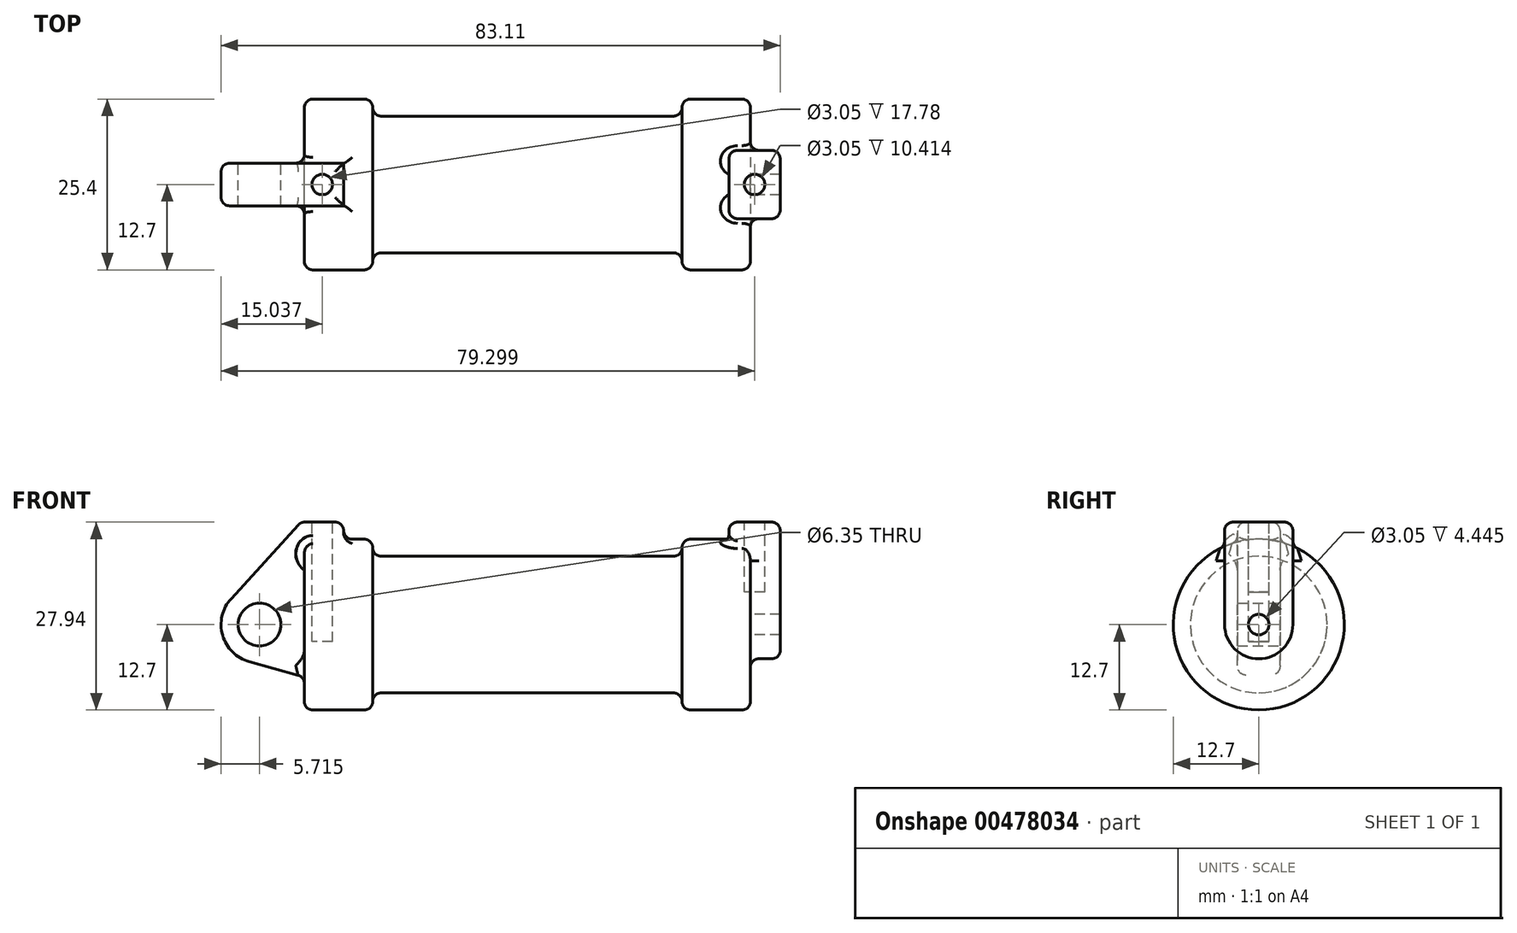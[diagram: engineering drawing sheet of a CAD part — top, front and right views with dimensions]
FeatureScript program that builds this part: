
annotation { "Feature Type Name" : "Feature", "Feature Type Description" : "" }
export const myFeature = defineFeature(function(context is Context, id is Id, definition is map)
    precondition{}
    {
        {
            var Q0;
            Q0=qCreatedBy(makeId("Front.planeOp"),FACE);
            var sketch = newSketch(context, id + "F0", { "sketchPlane" : qUnion([Q0])});
            skLineSegment(sketch, "E0", {"start": v(0, 0) * mm, "end": v(0, 12.7) * mm});
            skLineSegment(sketch, "E1", {"start": v(0, 12.7) * mm, "end": v(10.16, 12.7) * mm});
            skLineSegment(sketch, "E2", {"start": v(10.16, 12.7) * mm, "end": v(10.16, 10.16) * mm});
            skLineSegment(sketch, "E3", {"start": v(10.16, 10.16) * mm, "end": v(56.13, 10.16) * mm});
            skLineSegment(sketch, "E4", {"start": v(56.13, 10.16) * mm, "end": v(56.13, 12.7) * mm});
            skLineSegment(sketch, "E5", {"start": v(56.13, 12.7) * mm, "end": v(66.3, 12.7) * mm});
            skLineSegment(sketch, "E6", {"start": v(66.3, 12.7) * mm, "end": v(66.3, 0) * mm});
            skLineSegment(sketch, "E7", {"start": v(66.3, 0) * mm, "end": v(0, 0) * mm});
            skLineSegment(sketch, "E8", {"start": v(5.84, 15.24) * mm, "end": v(-0.5, 15.24) * mm});
            skLineSegment(sketch, "E9", {"start": v(-0.5, 15.24) * mm, "end": v(-10.88, 3.85) * mm});
            skLineSegment(sketch, "E10", {"start": v(0, 0) * mm, "end": v(-6.65, 0) * mm});
            skCircle(sketch, "E11", {"center": v(-6.65, 0) * mm, "radius": 5.72 * mm});
            skCircle(sketch, "E12", {"center": v(-6.65, 0) * mm, "radius": 3.18 * mm});
            skLineSegment(sketch, "E13", {"start": v(5.84, 15.24) * mm, "end": v(5.84, -9.4) * mm});
            skLineSegment(sketch, "E14", {"start": v(5.84, -9.4) * mm, "end": v(-8.18, -5.5) * mm});
            skSolve(sketch);
        }
        {
            var Q0;
            {var subQ0=sQuery(id+"F0.wireOp",EDGE,"E2");Q0=makeQuery(id+"F0.imprint","IMPRINT",FACE,{"disambiguationData":[TD([[makeQuery(id+"F0.imprint","IMPRINT",EDGE,{"derivedFrom":subQ0}),-1.0]])]});}
            var Q1;
            {var subQ0=sQuery(id+"F0.wireOp",EDGE,"E0");Q1=makeQuery(id+"F0.imprint","IMPRINT",FACE,{"disambiguationData":[TD([[makeQuery(id+"F0.imprint","IMPRINT",EDGE,{"derivedFrom":subQ0}),-1.0]])]});}
            var Q2;
            Q2=sQuery(id+"F0.wireOp",EDGE,"E7");
            revolve(context, id + "F1", {"entities" : qUnion([Q0, Q1]), "axis" : qUnion([Q2]), "revolveType" : RevolveType.FULL});
        }
        {
            var Q0;
            {var subQ1=sQuery(id+"F0.wireOp",EDGE,"E0");Q0=makeQuery(id+"F0.imprint","IMPRINT",FACE,{"disambiguationData":[TD([[makeQuery(id+"F0.imprint","IMPRINT",EDGE,{"derivedFrom":subQ1}),1.0]])]});}
            var Q1;
            {var subQ0=sQuery(id+"F0.wireOp",EDGE,"E0");Q1=makeQuery(id+"F0.imprint","IMPRINT",FACE,{"disambiguationData":[TD([[makeQuery(id+"F0.imprint","IMPRINT",EDGE,{"derivedFrom":subQ0}),-1.0]])]});}
            var Q2;
            {var subQ0=sQuery(id+"F0.wireOp",EDGE,"E14");Q2=makeQuery(id+"F0.imprint","IMPRINT",FACE,{"disambiguationData":[TD([[makeQuery(id+"F0.imprint","IMPRINT",EDGE,{"derivedFrom":subQ0}),-1.0]])]});}
            var Q3;
            {var subQ5=sQuery(id+"F0.wireOp",EDGE,"E12");Q3=makeQuery(id+"F0.imprint","IMPRINT",FACE,{"disambiguationData":[TD([[makeQuery(id+"F0.imprint","IMPRINT",EDGE,{"derivedFrom":subQ5}),-1.0]])]});}
            extrude(context, id + "F2", {"entities" : qUnion([Q0, Q1, Q2, Q3]), "operationType" : NewBodyOperationType.ADD, "endBound" : BoundingType.SYMMETRIC, "depth" : 6.35 * mm});
        }
        {
            var Q0;
            Q0=makeQuery(id+"F1.opRevolve","SWEPT_FACE",FACE,{"disambiguationData":[OSD([sQuery(id+"F0.wireOp",EDGE,"E6")])]});
            var sketch = newSketch(context, id + "F3", { "sketchPlane" : qUnion([Q0])});
            skCircle(sketch, "E15", {"center": v(0, 0) * mm, "radius": 1.52 * mm});
            skCircle(sketch, "E16", {"center": v(0, 0) * mm, "radius": 5.08 * mm});
            skLineSegment(sketch, "E17.0", {"start": v(-3.18, 15.24) * mm, "end": v(3.17, 15.24) * mm});
            skLineSegment(sketch, "E18", {"start": v(5.08, 0) * mm, "end": v(5.08, 15.24) * mm});
            skLineSegment(sketch, "E19", {"start": v(-5.08, 0) * mm, "end": v(-5.08, 15.24) * mm});
            skLineSegment(sketch, "E20", {"start": v(-5.08, 15.24) * mm, "end": v(5.08, 15.24) * mm});
            skSolve(sketch);
        }
        {
            var Q0;
            Q0=makeQuery(id+"F3.imprint","IMPRINT",FACE,{"disambiguationData":[TD([[makeQuery(id+"F3.imprint","IMPRINT",EDGE,{"derivedFrom":sQuery(id+"F3.wireOp",EDGE,"E15")}),-1.0]])]});
            var Q1;
            {var subQ0=sQuery(id+"F3.wireOp",EDGE,"E18");var subQ1=sQuery(id+"F3.wireOp",EDGE,"E16");var subQ2=makeQuery(id+"F3.imprint","INTERSECT",VERTEX,{"derivedFrom":[subQ1,subQ0]});Q1=makeQuery(id+"F3.imprint","IMPRINT",FACE,{"disambiguationData":[TD([[makeQuery(id+"F3.imprint","IMPRINT",EDGE,{"disambiguationData":[TD([[subQ2,-1.0]])],"derivedFrom":subQ1}),-1.0]])]});}
            var Q2;
            {var subQ0=sQuery(id+"F3.wireOp",EDGE,"E20");var subQ1=sQuery(id+"F3.wireOp",EDGE,"E18");var subQ2=makeQuery(id+"F3.imprint","INTERSECT",VERTEX,{"derivedFrom":[subQ1,subQ0]});Q2=makeQuery(id+"F3.imprint","IMPRINT",FACE,{"disambiguationData":[TD([[makeQuery(id+"F3.imprint","IMPRINT",EDGE,{"disambiguationData":[TD([[subQ2,1.0]])],"derivedFrom":subQ0}),-1.0]])]});}
            extrude(context, id + "F4", {"entities" : qUnion([Q0, Q1, Q2]), "operationType" : NewBodyOperationType.ADD, "endBound" : BoundingType.SYMMETRIC, "depth" : 6.35 * mm});
        }
        {
            var Q0;
            Q0=makeQuery(id+"F4.opExtrude","CAP_FACE",FACE,{"disambiguationData":[OSD([sQuery(id+"F3.wireOp",EDGE,"E15"),sQuery(id+"F3.wireOp",EDGE,"E16"),sQuery(id+"F3.wireOp",EDGE,"E18"),sQuery(id+"F3.wireOp",EDGE,"E19"),sQuery(id+"F3.wireOp",EDGE,"E20")])],"isStart":false});
            extrude(context, id + "F5", {"entities" : qUnion([Q0]), "operationType" : NewBodyOperationType.ADD, "depth" : 1.27 * mm});
        }
        {
            var Q0;
            Q0=makeQuery(id+"F4.boolean.opBoolean","SPLIT",FACE,{"disambiguationData":[TD([makeQuery(id+"F4.opExtrude","SWEPT_FACE",FACE,{"disambiguationData":[OSD([sQuery(id+"F3.wireOp",EDGE,"E15")])]})])],"derivedFrom":makeQuery(id+"F1.opRevolve","SWEPT_FACE",FACE,{"disambiguationData":[OSD([sQuery(id+"F0.wireOp",EDGE,"E6")])]})});
            extrude(context, id + "F6", {"entities" : qUnion([Q0]), "operationType" : NewBodyOperationType.ADD, "oppositeDirection" : true, "depth" : 60.45 * mm});
        }
        {
            var Q0;
            Q0=makeQuery(id+"F2.opExtrude","SWEPT_FACE",FACE,{"disambiguationData":[OSD([sQuery(id+"F0.wireOp",EDGE,"E8")])]});
            var sketch = newSketch(context, id + "F7", { "sketchPlane" : qUnion([Q0])});
            skCircle(sketch, "E21", {"center": v(2.67, 0) * mm, "radius": 1.52 * mm});
            skSolve(sketch);
        }
        {
            var Q0;
            Q0=makeQuery(id+"F7.imprint","IMPRINT",FACE,{"disambiguationData":[TD([[makeQuery(id+"F7.imprint","IMPRINT",EDGE,{"derivedFrom":sQuery(id+"F7.wireOp",EDGE,"E21")}),1.0]])]});
            var Q1;
            Q1=sQuery(id+"F7.wireOp",EDGE,"E21");
            extrude(context, id + "F8", {"entities" : qUnion([Q0]), "operationType" : NewBodyOperationType.REMOVE, "surfaceEntities" : qUnion([Q1]), "oppositeDirection" : true, "depth" : 17.78 * mm});
        }
        {
            var Q0;
            {var subQ0=sQuery(id+"F3.wireOp",EDGE,"E20");Q0=makeQuery(id+"F5.boolean.opBoolean","MERGE",FACE,{"derivedFrom":[makeQuery(id+"F4.opExtrude","SWEPT_FACE",FACE,{"disambiguationData":[OSD([subQ0])]}),makeQuery(id+"F5.opExtrude","SWEPT_FACE",FACE,{"disambiguationData":[OSD([subQ0])]})]});}
            var sketch = newSketch(context, id + "F9", { "sketchPlane" : qUnion([Q0])});
            skCircle(sketch, "E22", {"center": v(66.93, 0) * mm, "radius": 1.52 * mm});
            skSolve(sketch);
        }
        {
            var Q0;
            Q0 = qSketchRegion(id + "F9", true);
            extrude(context, id + "F10", {"entities" : qUnion([Q0]), "operationType" : NewBodyOperationType.REMOVE, "oppositeDirection" : true, "depth" : 10.4 * mm});
        }
        {
            var Q0;
            Q0=makeQuery(id+"F1.opRevolve","SWEPT_FACE",FACE,{"disambiguationData":[OSD([sQuery(id+"F0.wireOp",EDGE,"E3")])]});
            fillet(context, id + "F11", {"entities" : qUnion([Q0]), "radius" : 1.27 * mm, "tangentPropagation" : true, "allowEdgeOverflow" : false});
        }
        {
            var Q0;
            Q0=makeQuery(id+"F1.opRevolve","SWEPT_FACE",FACE,{"disambiguationData":[OSD([sQuery(id+"F0.wireOp",EDGE,"E1")])]});
            fillet(context, id + "F12", {"entities" : qUnion([Q0]), "radius" : 1.27 * mm, "tangentPropagation" : true, "allowEdgeOverflow" : false});
        }
        {
            var Q0;
            Q0=makeQuery(id+"F2.opExtrude","CAP_EDGE",EDGE,{"disambiguationData":[OSD([sQuery(id+"F0.wireOp",EDGE,"E8")])],"isStart":false});
            var Q1;
            Q1=makeQuery(id+"F2.opExtrude","SWEPT_EDGE",EDGE,{"disambiguationData":[OSD([sQuery(id+"F0.wireOp",EDGE,"E8"),sQuery(id+"F0.wireOp",EDGE,"E13")])]});
            var Q2;
            Q2=makeQuery(id+"F2.opExtrude","CAP_EDGE",EDGE,{"disambiguationData":[OSD([sQuery(id+"F0.wireOp",EDGE,"E8")])],"isStart":true});
            var Q3;
            Q3=makeQuery(id+"F2.opExtrude","SWEPT_EDGE",EDGE,{"disambiguationData":[OSD([sQuery(id+"F0.wireOp",EDGE,"E8"),sQuery(id+"F0.wireOp",EDGE,"E9")])]});
            var Q4;
            Q4=makeQuery(id+"F2.opExtrude","CAP_EDGE",EDGE,{"disambiguationData":[OSD([sQuery(id+"F0.wireOp",EDGE,"E9")])],"isStart":true});
            var Q5;
            Q5=makeQuery(id+"F2.opExtrude","CAP_EDGE",EDGE,{"disambiguationData":[OSD([sQuery(id+"F0.wireOp",EDGE,"E9")])],"isStart":false});
            var Q6;
            Q6=makeQuery(id+"F2.opExtrude","SWEPT_EDGE",EDGE,{"disambiguationData":[OSD([sQuery(id+"F0.wireOp",EDGE,"E9"),sQuery(id+"F0.wireOp",EDGE,"E11")])]});
            var Q7;
            Q7=makeQuery(id+"F2.opExtrude","CAP_EDGE",EDGE,{"disambiguationData":[OSD([sQuery(id+"F0.wireOp",EDGE,"E11")])],"isStart":false});
            var Q8;
            Q8=makeQuery(id+"F2.opExtrude","CAP_EDGE",EDGE,{"disambiguationData":[OSD([sQuery(id+"F0.wireOp",EDGE,"E11")])],"isStart":true});
            var Q9;
            Q9=makeQuery(id+"F2.opExtrude","CAP_EDGE",EDGE,{"disambiguationData":[OSD([sQuery(id+"F0.wireOp",EDGE,"E14")])],"isStart":true});
            var Q10;
            Q10=makeQuery(id+"F2.opExtrude","CAP_EDGE",EDGE,{"disambiguationData":[OSD([sQuery(id+"F0.wireOp",EDGE,"E14")])],"isStart":false});
            var Q11;
            {var subQ0=sQuery(id+"F0.wireOp",EDGE,"E14");Q11=makeQuery(id+"F12.opFillet","BLEND_EDGE",EDGE,{"blendedFrom":[makeQuery(id+"F2.boolean.opBoolean","INTERSECT",EDGE,{"derivedFrom":[makeQuery(id+"F1.opRevolve","SWEPT_FACE",FACE,{"disambiguationData":[OSD([sQuery(id+"F0.wireOp",EDGE,"E0")])]}),makeQuery(id+"F2.opExtrude","CAP_FACE",FACE,{"disambiguationData":[OSD([sQuery(id+"F0.wireOp",EDGE,"E8"),sQuery(id+"F0.wireOp",EDGE,"E9"),sQuery(id+"F0.wireOp",EDGE,"E11"),sQuery(id+"F0.wireOp",EDGE,"E12"),sQuery(id+"F0.wireOp",EDGE,"E13"),subQ0])],"isStart":false})]}),makeQuery(id+"F2.opExtrude","SWEPT_FACE",FACE,{"disambiguationData":[OSD([subQ0])]})],"blendedInto":[makeQuery(id+"F2.opExtrude","SWEPT_FACE",FACE,{"disambiguationData":[OSD([subQ0])]})]});}
            var Q12;
            {var subQ0=sQuery(id+"F0.wireOp",EDGE,"E14");Q12=makeQuery(id+"F12.opFillet","BLEND_EDGE",EDGE,{"blendedFrom":[makeQuery(id+"F2.boolean.opBoolean","INTERSECT",EDGE,{"derivedFrom":[makeQuery(id+"F1.opRevolve","SWEPT_FACE",FACE,{"disambiguationData":[OSD([sQuery(id+"F0.wireOp",EDGE,"E0")])]}),makeQuery(id+"F2.opExtrude","CAP_FACE",FACE,{"disambiguationData":[OSD([sQuery(id+"F0.wireOp",EDGE,"E8"),sQuery(id+"F0.wireOp",EDGE,"E9"),sQuery(id+"F0.wireOp",EDGE,"E11"),sQuery(id+"F0.wireOp",EDGE,"E12"),sQuery(id+"F0.wireOp",EDGE,"E13"),subQ0])],"isStart":true})]}),makeQuery(id+"F2.opExtrude","SWEPT_FACE",FACE,{"disambiguationData":[OSD([subQ0])]})],"blendedInto":[makeQuery(id+"F2.opExtrude","SWEPT_FACE",FACE,{"disambiguationData":[OSD([subQ0])]})]});}
            var Q13;
            Q13=makeQuery(id+"F2.boolean.opBoolean","INTERSECT",EDGE,{"derivedFrom":[makeQuery(id+"F1.opRevolve","SWEPT_FACE",FACE,{"disambiguationData":[OSD([sQuery(id+"F0.wireOp",EDGE,"E0")])]}),makeQuery(id+"F2.opExtrude","SWEPT_FACE",FACE,{"disambiguationData":[OSD([sQuery(id+"F0.wireOp",EDGE,"E14")])]})]});
            fillet(context, id + "F13", {"entities" : qUnion([Q0, Q1, Q2, Q3, Q4, Q5, Q6, Q7, Q8, Q9, Q10, Q11, Q12, Q13]), "radius" : 1.27 * mm, "tangentPropagation" : true, "allowEdgeOverflow" : false});
        }
        {
            var Q0;
            Q0=makeQuery(id+"F1.opRevolve","SWEPT_EDGE",EDGE,{"disambiguationData":[OSD([sQuery(id+"F0.wireOp",EDGE,"E5"),sQuery(id+"F0.wireOp",EDGE,"E6")])]});
            fillet(context, id + "F14", {"entities" : qUnion([Q0]), "radius" : 1.27 * mm, "tangentPropagation" : true, "allowEdgeOverflow" : false});
        }
        {
            var Q0;
            Q0=makeQuery(id+"F4.opExtrude","CAP_EDGE",EDGE,{"disambiguationData":[OSD([sQuery(id+"F3.wireOp",EDGE,"E18")])],"isStart":true});
            var Q1;
            Q1=makeQuery(id+"F4.boolean.opBoolean","INTERSECT",EDGE,{"derivedFrom":[makeQuery(id+"F1.opRevolve","SWEPT_FACE",FACE,{"disambiguationData":[OSD([sQuery(id+"F0.wireOp",EDGE,"E5")])]}),makeQuery(id+"F4.opExtrude","SWEPT_FACE",FACE,{"disambiguationData":[OSD([sQuery(id+"F3.wireOp",EDGE,"E18")])]})]});
            var Q2;
            {var subQ0=sQuery(id+"F3.wireOp",EDGE,"E18");Q2=makeQuery(id+"F14.opFillet","BLEND_EDGE",EDGE,{"blendedFrom":[makeQuery(id+"F1.opRevolve","SWEPT_EDGE",EDGE,{"disambiguationData":[OSD([sQuery(id+"F0.wireOp",EDGE,"E5"),sQuery(id+"F0.wireOp",EDGE,"E6")])]}),makeQuery(id+"F5.boolean.opBoolean","MERGE",FACE,{"derivedFrom":[makeQuery(id+"F4.opExtrude","SWEPT_FACE",FACE,{"disambiguationData":[OSD([subQ0])]}),makeQuery(id+"F5.opExtrude","SWEPT_FACE",FACE,{"disambiguationData":[OSD([subQ0])]})]})],"blendedInto":[makeQuery(id+"F5.boolean.opBoolean","MERGE",FACE,{"derivedFrom":[makeQuery(id+"F4.opExtrude","SWEPT_FACE",FACE,{"disambiguationData":[OSD([subQ0])]}),makeQuery(id+"F5.opExtrude","SWEPT_FACE",FACE,{"disambiguationData":[OSD([subQ0])]})]})]});}
            var Q3;
            Q3=makeQuery(id+"F4.boolean.opBoolean","INTERSECT",EDGE,{"derivedFrom":[makeQuery(id+"F1.opRevolve","SWEPT_FACE",FACE,{"disambiguationData":[OSD([sQuery(id+"F0.wireOp",EDGE,"E6")])]}),makeQuery(id+"F4.opExtrude","SWEPT_FACE",FACE,{"disambiguationData":[OSD([sQuery(id+"F3.wireOp",EDGE,"E18")])]})]});
            var Q4;
            Q4=makeQuery(id+"F4.boolean.opBoolean","INTERSECT",EDGE,{"derivedFrom":[makeQuery(id+"F1.opRevolve","SWEPT_FACE",FACE,{"disambiguationData":[OSD([sQuery(id+"F0.wireOp",EDGE,"E6")])]}),makeQuery(id+"F4.opExtrude","SWEPT_FACE",FACE,{"disambiguationData":[OSD([sQuery(id+"F3.wireOp",EDGE,"E16")])]})]});
            var Q5;
            Q5=makeQuery(id+"F4.boolean.opBoolean","INTERSECT",EDGE,{"derivedFrom":[makeQuery(id+"F1.opRevolve","SWEPT_FACE",FACE,{"disambiguationData":[OSD([sQuery(id+"F0.wireOp",EDGE,"E6")])]}),makeQuery(id+"F4.opExtrude","SWEPT_FACE",FACE,{"disambiguationData":[OSD([sQuery(id+"F3.wireOp",EDGE,"E19")])]})]});
            var Q6;
            {var subQ0=sQuery(id+"F3.wireOp",EDGE,"E19");Q6=makeQuery(id+"F14.opFillet","BLEND_EDGE",EDGE,{"blendedFrom":[makeQuery(id+"F1.opRevolve","SWEPT_EDGE",EDGE,{"disambiguationData":[OSD([sQuery(id+"F0.wireOp",EDGE,"E5"),sQuery(id+"F0.wireOp",EDGE,"E6")])]}),makeQuery(id+"F5.boolean.opBoolean","MERGE",FACE,{"derivedFrom":[makeQuery(id+"F4.opExtrude","SWEPT_FACE",FACE,{"disambiguationData":[OSD([subQ0])]}),makeQuery(id+"F5.opExtrude","SWEPT_FACE",FACE,{"disambiguationData":[OSD([subQ0])]})]})],"blendedInto":[makeQuery(id+"F5.boolean.opBoolean","MERGE",FACE,{"derivedFrom":[makeQuery(id+"F4.opExtrude","SWEPT_FACE",FACE,{"disambiguationData":[OSD([subQ0])]}),makeQuery(id+"F5.opExtrude","SWEPT_FACE",FACE,{"disambiguationData":[OSD([subQ0])]})]})]});}
            var Q7;
            Q7=makeQuery(id+"F4.boolean.opBoolean","INTERSECT",EDGE,{"derivedFrom":[makeQuery(id+"F1.opRevolve","SWEPT_FACE",FACE,{"disambiguationData":[OSD([sQuery(id+"F0.wireOp",EDGE,"E5")])]}),makeQuery(id+"F4.opExtrude","SWEPT_FACE",FACE,{"disambiguationData":[OSD([sQuery(id+"F3.wireOp",EDGE,"E19")])]})]});
            var Q8;
            Q8=makeQuery(id+"F4.opExtrude","CAP_EDGE",EDGE,{"disambiguationData":[OSD([sQuery(id+"F3.wireOp",EDGE,"E19")])],"isStart":true});
            var Q9;
            {var subQ0=sQuery(id+"F3.wireOp",EDGE,"E20");var subQ1=sQuery(id+"F3.wireOp",EDGE,"E19");Q9=makeQuery(id+"F5.boolean.opBoolean","MERGE",EDGE,{"derivedFrom":[makeQuery(id+"F4.opExtrude","SWEPT_EDGE",EDGE,{"disambiguationData":[OSD([subQ1,subQ0])]}),makeQuery(id+"F5.opExtrude","SWEPT_EDGE",EDGE,{"disambiguationData":[OSD([subQ1,subQ0])]})]});}
            var Q10;
            Q10=makeQuery(id+"F5.opExtrude","CAP_EDGE",EDGE,{"disambiguationData":[OSD([sQuery(id+"F3.wireOp",EDGE,"E19")])],"isStart":false});
            var Q11;
            Q11=makeQuery(id+"F5.opExtrude","CAP_EDGE",EDGE,{"disambiguationData":[OSD([sQuery(id+"F3.wireOp",EDGE,"E20")])],"isStart":false});
            var Q12;
            Q12=makeQuery(id+"F5.opExtrude","CAP_EDGE",EDGE,{"disambiguationData":[OSD([sQuery(id+"F3.wireOp",EDGE,"E18")])],"isStart":false});
            var Q13;
            Q13=makeQuery(id+"F5.opExtrude","CAP_EDGE",EDGE,{"disambiguationData":[OSD([sQuery(id+"F3.wireOp",EDGE,"E16")])],"isStart":false});
            var Q14;
            Q14=makeQuery(id+"F4.opExtrude","CAP_EDGE",EDGE,{"disambiguationData":[OSD([sQuery(id+"F3.wireOp",EDGE,"E20")])],"isStart":true});
            fillet(context, id + "F15", {"entities" : qUnion([Q0, Q1, Q2, Q3, Q4, Q5, Q6, Q7, Q8, Q9, Q10, Q11, Q12, Q13, Q14]), "radius" : 1.27 * mm, "tangentPropagation" : true, "allowEdgeOverflow" : false});
        }
        {
            var Q0;
            {var subQ0=sQuery(id+"F3.wireOp",EDGE,"E20");var subQ1=sQuery(id+"F3.wireOp",EDGE,"E18");Q0=makeQuery(id+"F5.boolean.opBoolean","MERGE",EDGE,{"derivedFrom":[makeQuery(id+"F4.opExtrude","SWEPT_EDGE",EDGE,{"disambiguationData":[OSD([subQ1,subQ0])]}),makeQuery(id+"F5.opExtrude","SWEPT_EDGE",EDGE,{"disambiguationData":[OSD([subQ1,subQ0])]})]});}
            fillet(context, id + "F16", {"entities" : qUnion([Q0]), "radius" : 1.27 * mm, "tangentPropagation" : true, "allowEdgeOverflow" : false});
        }
        {
            var Q0;
            Q0=makeQuery(id+"F1.opRevolve","SWEPT_EDGE",EDGE,{"disambiguationData":[OSD([sQuery(id+"F0.wireOp",EDGE,"E4"),sQuery(id+"F0.wireOp",EDGE,"E5")])]});
            fillet(context, id + "F17", {"entities" : qUnion([Q0]), "radius" : 1.27 * mm, "tangentPropagation" : true, "allowEdgeOverflow" : false});
        }
    });
